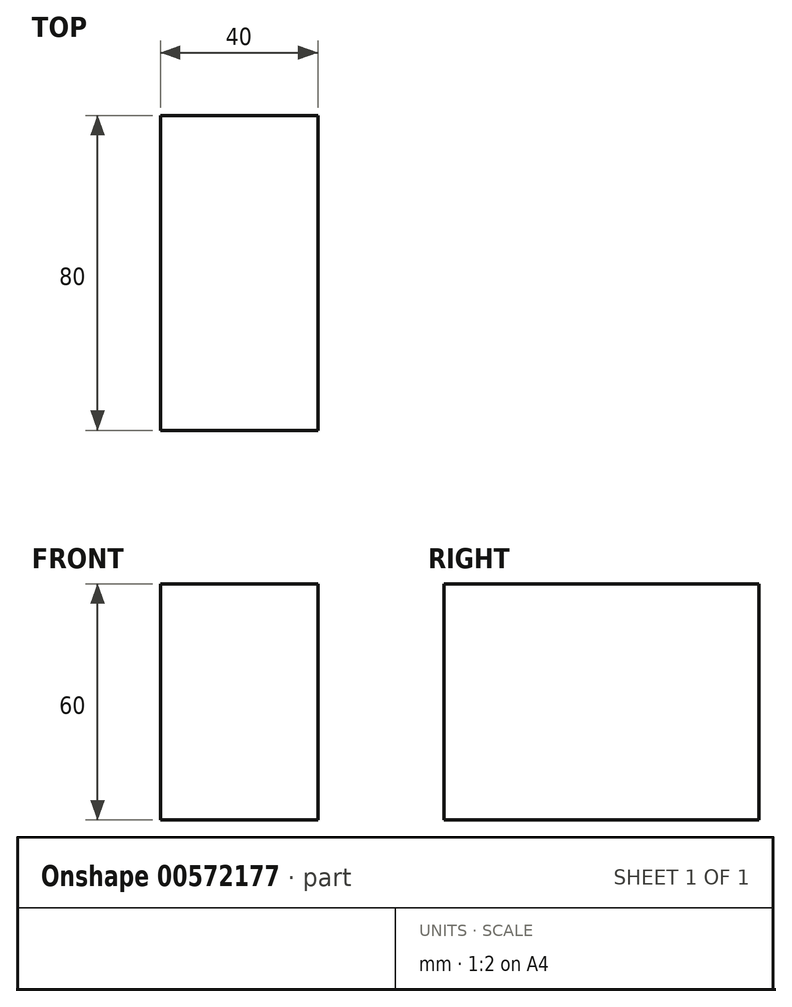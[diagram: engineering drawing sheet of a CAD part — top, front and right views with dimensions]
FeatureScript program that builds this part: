
annotation { "Feature Type Name" : "Feature", "Feature Type Description" : "" }
export const myFeature = defineFeature(function(context is Context, id is Id, definition is map)
    precondition{}
    {
        {
            var Q0;
            Q0=qCreatedBy(makeId("Front.planeOp"),FACE);
            var sketch = newSketch(context, id + "F0", { "sketchPlane" : qUnion([Q0])});
            skLineSegment(sketch, "E0.bottom", {"start": v(0, 0) * mm, "end": v(40, 0) * mm});
            skLineSegment(sketch, "E0.top", {"start": v(0, 60) * mm, "end": v(40, 60) * mm});
            skLineSegment(sketch, "E0.left", {"start": v(0, 0) * mm, "end": v(0, 60) * mm});
            skLineSegment(sketch, "E0.right", {"start": v(40, 0) * mm, "end": v(40, 60) * mm});
            skSolve(sketch);
        }
        {
            var Q0;
            Q0=makeQuery(id+"F0.imprint","IMPRINT",FACE,{"disambiguationData":[TD([[makeQuery(id+"F0.imprint","IMPRINT",EDGE,{"derivedFrom":sQuery(id+"F0.wireOp",EDGE,"E0.bottom")}),1.0]])]});
            extrude(context, id + "F1", {"entities" : qUnion([Q0]), "depth" : 80 * mm, "offsetDistance" : 25 * mm});
        }
    });
